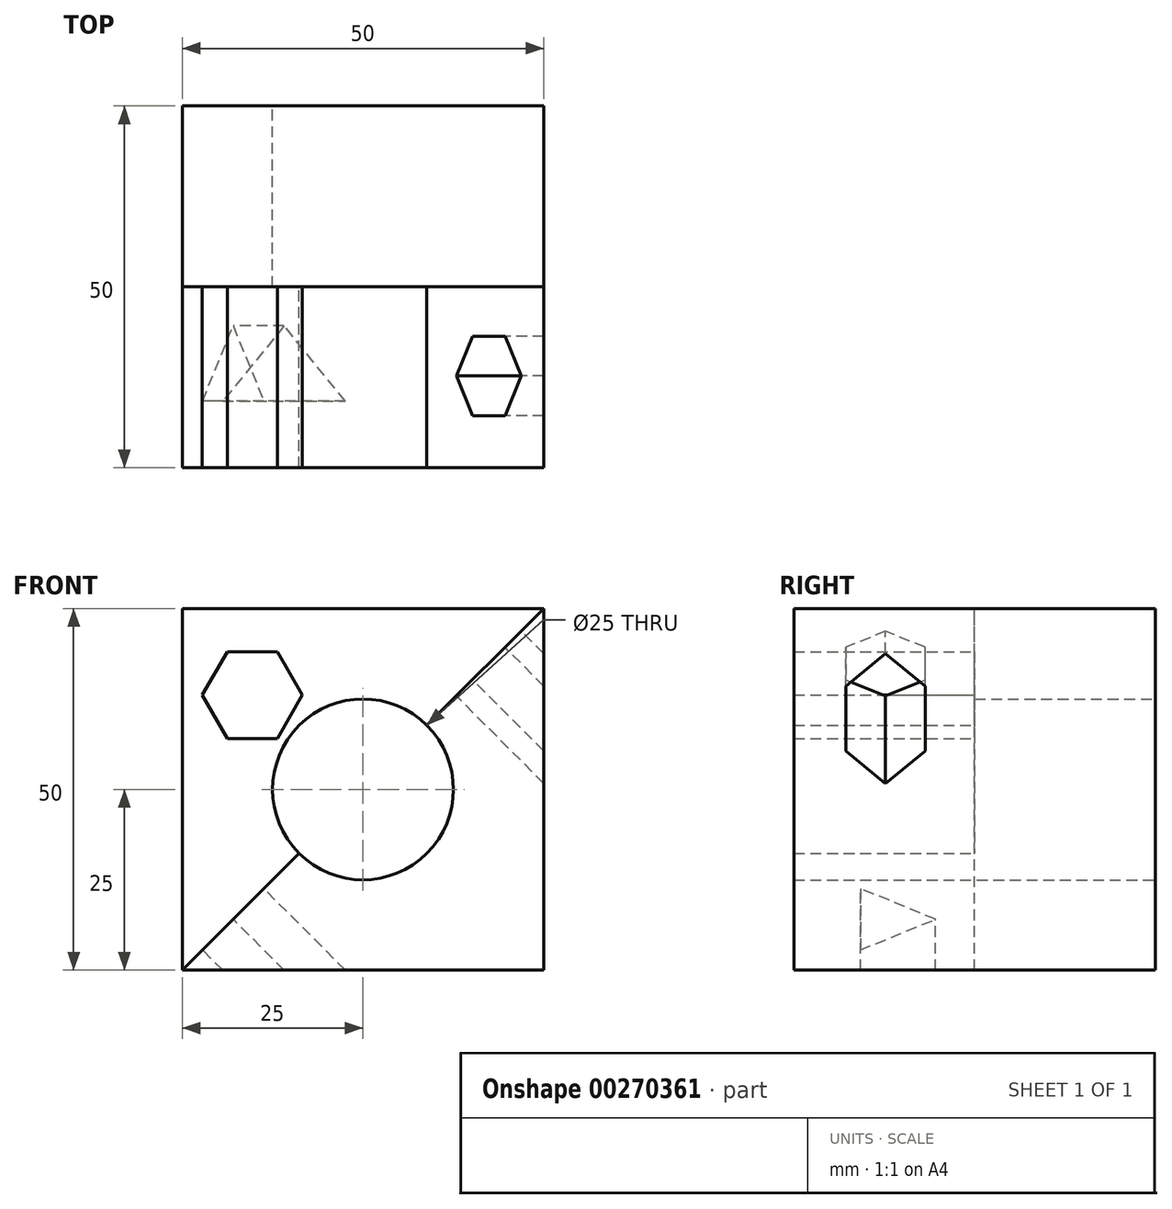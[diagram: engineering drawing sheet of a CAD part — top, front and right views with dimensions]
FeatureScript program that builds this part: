
annotation { "Feature Type Name" : "Feature", "Feature Type Description" : "" }
export const myFeature = defineFeature(function(context is Context, id is Id, definition is map)
    precondition{}
    {
        {
            var Q0;
            Q0=qCreatedBy(makeId("Front.planeOp"),FACE);
            var sketch = newSketch(context, id + "F0", { "sketchPlane" : qUnion([Q0])});
            skLineSegment(sketch, "E0.bottom", {"start": v(25, -25) * mm, "end": v(-25, -25) * mm});
            skLineSegment(sketch, "E0.top", {"start": v(25, 25) * mm, "end": v(-25, 25) * mm});
            skLineSegment(sketch, "E0.left", {"start": v(25, -25) * mm, "end": v(25, 25) * mm});
            skLineSegment(sketch, "E0.right", {"start": v(-25, -25) * mm, "end": v(-25, 25) * mm});
            skPoint(sketch, "E0.middle", {"position": v(0, 0) * mm});
            skCircle(sketch, "E1", {"center": v(0, 0) * mm, "radius": 12.5 * mm});
            skSolve(sketch);
        }
        {
            var Q0;
            Q0=makeQuery(id+"F0.imprint","IMPRINT",FACE,{"disambiguationData":[TD([[makeQuery(id+"F0.imprint","IMPRINT",EDGE,{"derivedFrom":sQuery(id+"F0.wireOp",EDGE,"E0.bottom")}),-1.0]])]});
            extrude(context, id + "F1", {"entities" : qUnion([Q0]), "depth" : 25 * mm});
        }
        {
            var Q0;
            Q0=makeQuery(id+"F1.opExtrude","CAP_FACE",FACE,{"disambiguationData":[OSD([sQuery(id+"F0.wireOp",EDGE,"E0.bottom"),sQuery(id+"F0.wireOp",EDGE,"E0.top"),sQuery(id+"F0.wireOp",EDGE,"E0.left"),sQuery(id+"F0.wireOp",EDGE,"E0.right"),sQuery(id+"F0.wireOp",EDGE,"E1")])],"isStart":false});
            var sketch = newSketch(context, id + "F2", { "sketchPlane" : qUnion([Q0])});
            skLineSegment(sketch, "E2", {"start": v(-25, -25) * mm, "end": v(-8.84, -8.84) * mm});
            skLineSegment(sketch, "E3", {"start": v(25, 25) * mm, "end": v(25, -25) * mm});
            skLineSegment(sketch, "E4", {"start": v(25, -25) * mm, "end": v(-25, -25) * mm});
            skCircle(sketch, "E5", {"center": v(0, 0) * mm, "radius": 12.5 * mm});
            skLineSegment(sketch, "E6.trimOffspring", {"start": v(8.84, 8.84) * mm, "end": v(25, 25) * mm});
            skSolve(sketch);
        }
        {
            var Q0;
            {var subQ1=sQuery(id+"F2.wireOp",EDGE,"E2");Q0=makeQuery(id+"F2.imprint","IMPRINT",FACE,{"disambiguationData":[TD([[makeQuery(id+"F2.imprint","IMPRINT",EDGE,{"derivedFrom":subQ1}),-1.0]])]});}
            extrude(context, id + "F3", {"entities" : qUnion([Q0]), "operationType" : NewBodyOperationType.ADD, "depth" : 25 * mm});
        }
        {
            var Q0;
            Q0=makeQuery(id+"F3.opExtrude","SWEPT_FACE",FACE,{"disambiguationData":[OSD([sQuery(id+"F2.wireOp",EDGE,"E2")])]});
            var sketch = newSketch(context, id + "F4", { "sketchPlane" : qUnion([Q0])});
            skCircle(sketch, "E7.cCircle", {"center": v(37.33, -25.4) * mm, "radius": 3.46 * mm, "construction": true});
            skLineSegment(sketch, "E7.0", {"start": v(40.8, -19.4) * mm, "end": v(40.8, -31.4) * mm});
            skLineSegment(sketch, "E7.1", {"start": v(40.8, -31.4) * mm, "end": v(30.4, -25.4) * mm});
            skLineSegment(sketch, "E7.2", {"start": v(30.4, -25.4) * mm, "end": v(40.8, -19.4) * mm});
            skPoint(sketch, "E7.0.midPoint", {"position": v(40.8, -25.4) * mm});
            skCircle(sketch, "E8.cCircle", {"center": v(37.33, 24.6) * mm, "radius": 5.5 * mm, "construction": true});
            skLineSegment(sketch, "E8.0", {"start": v(42.83, 27.78) * mm, "end": v(42.83, 21.43) * mm});
            skLineSegment(sketch, "E8.1", {"start": v(42.83, 21.43) * mm, "end": v(37.33, 18.26) * mm});
            skLineSegment(sketch, "E8.2", {"start": v(37.33, 18.26) * mm, "end": v(31.84, 21.43) * mm});
            skLineSegment(sketch, "E8.3", {"start": v(31.84, 21.43) * mm, "end": v(31.84, 27.78) * mm});
            skLineSegment(sketch, "E8.4", {"start": v(31.84, 27.78) * mm, "end": v(37.33, 30.95) * mm});
            skLineSegment(sketch, "E8.5", {"start": v(37.33, 30.95) * mm, "end": v(42.83, 27.78) * mm});
            skPoint(sketch, "E8.0.midPoint", {"position": v(42.83, 24.6) * mm});
            skSolve(sketch);
        }
        {
            var Q0;
            Q0 = qSketchRegion(id + "F4", true);
            extrude(context, id + "F5", {"entities" : qUnion([Q0]), "operationType" : NewBodyOperationType.REMOVE, "oppositeDirection" : true, "depth" : 50 * mm});
        }
        {
            var Q0;
            Q0=makeQuery(id+"F1.opExtrude","CAP_FACE",FACE,{"disambiguationData":[OSD([sQuery(id+"F0.wireOp",EDGE,"E0.bottom"),sQuery(id+"F0.wireOp",EDGE,"E0.top"),sQuery(id+"F0.wireOp",EDGE,"E0.left"),sQuery(id+"F0.wireOp",EDGE,"E0.right"),sQuery(id+"F0.wireOp",EDGE,"E1")])],"isStart":false});
            var sketch = newSketch(context, id + "F6", { "sketchPlane" : qUnion([Q0])});
            skCircle(sketch, "E9.cCircle", {"center": v(-15.31, 13.04) * mm, "radius": 5.99 * mm, "construction": true});
            skLineSegment(sketch, "E9.0", {"start": v(-18.77, 19.02) * mm, "end": v(-11.86, 19.02) * mm});
            skLineSegment(sketch, "E9.1", {"start": v(-11.86, 19.02) * mm, "end": v(-8.4, 13.04) * mm});
            skLineSegment(sketch, "E9.2", {"start": v(-8.4, 13.04) * mm, "end": v(-11.86, 7.05) * mm});
            skLineSegment(sketch, "E9.3", {"start": v(-11.86, 7.05) * mm, "end": v(-18.77, 7.05) * mm});
            skLineSegment(sketch, "E9.4", {"start": v(-18.77, 7.05) * mm, "end": v(-22.23, 13.04) * mm});
            skLineSegment(sketch, "E9.5", {"start": v(-22.23, 13.04) * mm, "end": v(-18.77, 19.02) * mm});
            skPoint(sketch, "E9.0.midPoint", {"position": v(-15.31, 19.02) * mm});
            skSolve(sketch);
        }
        {
            var Q0;
            Q0 = qSketchRegion(id + "F6", true);
            extrude(context, id + "F7", {"entities" : qUnion([Q0]), "operationType" : NewBodyOperationType.ADD, "depth" : 25 * mm});
        }
    });
